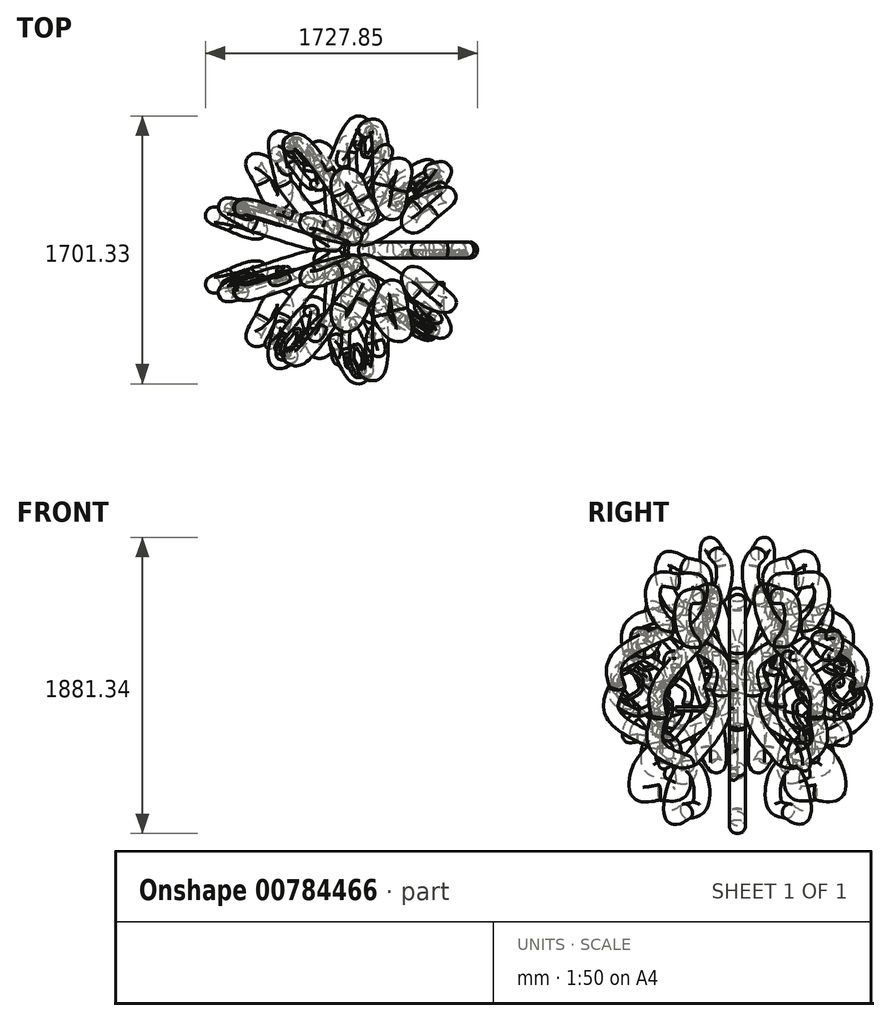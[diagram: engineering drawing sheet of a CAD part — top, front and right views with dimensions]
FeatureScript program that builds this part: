
annotation { "Feature Type Name" : "Feature", "Feature Type Description" : "" }
export const myFeature = defineFeature(function(context is Context, id is Id, definition is map)
    precondition{}
    {
        {
            var Q0;
            Q0=qCreatedBy(makeId("Top.planeOp"),FACE);
            var sketch = newSketch(context, id + "F0", { "sketchPlane" : qUnion([Q0])});
            skEllipse(sketch, "E0", {"center": v(0, 0) * mm, "majorRadius": 51.08 * mm, "minorRadius": 47.34 * mm, "majorAxis": v(-0.2, -0.98)});
            skSolve(sketch);
        }
        {
            var Q0;
            Q0=qCreatedBy(makeId("Front.planeOp"),FACE);
            var sketch = newSketch(context, id + "F1", { "sketchPlane" : qUnion([Q0])});
            skFitSpline(sketch, "E1", {"points": [v(0, 0) * mm, v(0, 227.77) * mm, v(209.25, 339.23) * mm, v(471.17, 411.68) * mm, v(599.35, 548.2) * mm, v(610.5, 656.88) * mm, v(487.9, 693.1) * mm], "startDerivative": vector(-275.49, 1390.88) * mm, "endDerivative": vector(-1128.05, 106.2) * mm});
            skSolve(sketch);
        }
        {
            var Q0;
            Q0=makeQuery(id+"F0.imprint","IMPRINT",FACE,{"disambiguationData":[TD([[makeQuery(id+"F0.imprint","IMPRINT",EDGE,{"derivedFrom":sQuery(id+"F0.wireOp",EDGE,"E0")}),1.0]])]});
            var Q1;
            Q1=sQuery(id+"F1.wireOp",EDGE,"E1");
            sweep(context, id + "F2", {"profiles" : qUnion([Q0]), "path" : qUnion([Q1])});
        }
        {
            var Q0;
            Q0=makeQuery(id+"F2.opSweep","SWEPT_BODY",BODY,{"disambiguationData":[OSD([sQuery(id+"F0.wireOp",EDGE,"E0"),sQuery(id+"F1.wireOp",EDGE,"E1")])]});
            var Q1;
            Q1=makeQuery(id+"F2.opSweep","CAP_FACE",FACE,{"disambiguationData":[OSD([sQuery(id+"F0.wireOp",EDGE,"E0"),sQuery(id+"F1.wireOp",VERTEX,"E1.end")])],"isStart":false});
            mirror(context, id + "F3", {"operationType" : NewBodyOperationType.ADD, "entities" : qUnion([Q0]), "mirrorPlane" : qUnion([Q1])});
        }
        {
            var Q0;
            Q0=qCreatedBy(makeId("Front.planeOp"),FACE);
            var sketch = newSketch(context, id + "F4", { "sketchPlane" : qUnion([Q0])});
            skLineSegment(sketch, "E2", {"start": v(788.67, -179) * mm, "end": v(-324.82, 201.02) * mm});
            skLineSegment(sketch, "E3", {"start": v(-324.82, 201.02) * mm, "end": v(-243.9, -248.34) * mm});
            skLineSegment(sketch, "E4", {"start": v(-243.9, -248.34) * mm, "end": v(620.3, -334.33) * mm});
            skLineSegment(sketch, "E5", {"start": v(620.3, -334.33) * mm, "end": v(788.67, -179) * mm});
            skSolve(sketch);
        }
        {
            var Q0;
            Q0 = qSketchRegion(id + "F4", true);
            extrude(context, id + "F5", {"entities" : qUnion([Q0]), "operationType" : NewBodyOperationType.REMOVE, "endBound" : BoundingType.SYMMETRIC, "depth" : 300 * mm, "offsetDistance" : 25 * mm});
        }
        {
            var Q0;
            Q0=makeQuery(id+"F2.opSweep","SWEPT_BODY",BODY,{"disambiguationData":[OSD([sQuery(id+"F0.wireOp",EDGE,"E0"),sQuery(id+"F1.wireOp",EDGE,"E1")])]});
            var Q1;
            Q1=makeQuery(id+"F5.boolean.opBoolean","COPY",FACE,{"disambiguationData":[TD([makeQuery(id+"F3.opPattern","COPY",FACE,{"derivedFrom":makeQuery(id+"F2.opSweep","SWEPT_FACE",FACE,{"disambiguationData":[OSD([sQuery(id+"F0.wireOp",EDGE,"E0"),sQuery(id+"F1.wireOp",EDGE,"E1")])]}),"instanceName":"1"})])],"derivedFrom":makeQuery(id+"F5.opExtrude","SWEPT_FACE",FACE,{"disambiguationData":[OSD([sQuery(id+"F4.wireOp",EDGE,"E2")])]})});
            mirror(context, id + "F6", {"operationType" : NewBodyOperationType.ADD, "entities" : qUnion([Q0]), "mirrorPlane" : qUnion([Q1])});
        }
        {
            var Q0;
            {var subQ0=sQuery(id+"F0.wireOp",EDGE,"E0");var subQ1=makeQuery(id+"F2.opSweep","SWEPT_FACE",FACE,{"disambiguationData":[OSD([subQ0,sQuery(id+"F1.wireOp",EDGE,"E1")])]});var subQ2=makeQuery(id+"F3.opPattern","COPY",FACE,{"derivedFrom":subQ1,"instanceName":"1"});var subQ3=makeQuery(id+"F5.boolean.opBoolean","INTERSECT",EDGE,{"derivedFrom":[makeQuery(id+"F3.boolean.opBoolean","SPLIT",FACE,{"disambiguationData":[TD([subQ1,makeQuery(id+"F3.opPattern","COPY",FACE,{"derivedFrom":makeQuery(id+"F2.opSweep","CAP_FACE",FACE,{"disambiguationData":[OSD([subQ0,sQuery(id+"F1.wireOp",VERTEX,"E1.start")])],"isStart":true}),"instanceName":"1"}),subQ2])],"derivedFrom":subQ2}),makeQuery(id+"F5.opExtrude","SWEPT_FACE",FACE,{"disambiguationData":[OSD([sQuery(id+"F4.wireOp",EDGE,"E2")])]})]});Q0=makeQuery(id+"F6.boolean.opBoolean","MERGE",EDGE,{"derivedFrom":[subQ3,makeQuery(id+"F6.opPattern","COPY",EDGE,{"derivedFrom":subQ3,"instanceName":"1"})]});}
            fillet(context, id + "F7", {"entities" : qUnion([Q0]), "radius" : 15 * mm, "tangentPropagation" : true, "allowEdgeOverflow" : false});
        }
        {
            var Q0;
            Q0=makeQuery(id+"F2.opSweep","SWEPT_BODY",BODY,{"disambiguationData":[OSD([sQuery(id+"F0.wireOp",EDGE,"E0"),sQuery(id+"F1.wireOp",EDGE,"E1")])]});
            var Q1;
            {var subQ0=sQuery(id+"F0.wireOp",EDGE,"E0");var subQ1=makeQuery(id+"F2.opSweep","SWEPT_FACE",FACE,{"disambiguationData":[OSD([subQ0,sQuery(id+"F1.wireOp",EDGE,"E1")])]});var subQ2=makeQuery(id+"F3.opPattern","COPY",FACE,{"derivedFrom":subQ1,"instanceName":"1"});var subQ3=makeQuery(id+"F3.boolean.opBoolean","SPLIT",FACE,{"disambiguationData":[TD([subQ1,makeQuery(id+"F3.opPattern","COPY",FACE,{"derivedFrom":makeQuery(id+"F2.opSweep","CAP_FACE",FACE,{"disambiguationData":[OSD([subQ0,sQuery(id+"F1.wireOp",VERTEX,"E1.start")])],"isStart":true}),"instanceName":"1"}),subQ2])],"derivedFrom":subQ2});var subQ4=subQ3;var subQ5=makeQuery(id+"F5.boolean.opBoolean","INTERSECT",EDGE,{"derivedFrom":[subQ3,makeQuery(id+"F5.opExtrude","SWEPT_FACE",FACE,{"disambiguationData":[OSD([sQuery(id+"F4.wireOp",EDGE,"E2")])]})]});Q1=makeQuery(id+"F7.opFillet","BLEND_VERTEX",VERTEX,{"disambiguationData":[OD(0.0)],"blendedFrom":[makeQuery(id+"F6.boolean.opBoolean","MERGE",EDGE,{"derivedFrom":[subQ5,makeQuery(id+"F6.opPattern","COPY",EDGE,{"derivedFrom":subQ5,"instanceName":"1"})]}),subQ4,makeQuery(id+"F6.opPattern","COPY",FACE,{"derivedFrom":subQ4,"instanceName":"1"})],"blendedInto":[subQ4,makeQuery(id+"F6.opPattern","COPY",FACE,{"derivedFrom":subQ4,"instanceName":"1"})]});}
            transform(context, id + "F8", {"entities" : qUnion([Q0]), "transformType" : TransformType.SCALE_UNIFORMLY, "scale" : 0.5, "scalePoint" : qUnion([Q1]), "makeCopy" : true});
        }
        {
            var Q0;
            Q0=makeQuery(id+"F8.opPattern","COPY",BODY,{"derivedFrom":makeQuery(id+"F2.opSweep","SWEPT_BODY",BODY,{"disambiguationData":[OSD([sQuery(id+"F0.wireOp",EDGE,"E0"),sQuery(id+"F1.wireOp",EDGE,"E1")])]}),"instanceName":"1"});
            var Q1;
            {var subQ0=sQuery(id+"F0.wireOp",EDGE,"E0");var subQ1=makeQuery(id+"F2.opSweep","SWEPT_FACE",FACE,{"disambiguationData":[OSD([subQ0,sQuery(id+"F1.wireOp",EDGE,"E1")])]});var subQ2=makeQuery(id+"F3.opPattern","COPY",FACE,{"derivedFrom":subQ1,"instanceName":"1"});var subQ3=makeQuery(id+"F3.boolean.opBoolean","SPLIT",FACE,{"disambiguationData":[TD([subQ1,makeQuery(id+"F3.opPattern","COPY",FACE,{"derivedFrom":makeQuery(id+"F2.opSweep","CAP_FACE",FACE,{"disambiguationData":[OSD([subQ0,sQuery(id+"F1.wireOp",VERTEX,"E1.start")])],"isStart":true}),"instanceName":"1"}),subQ2])],"derivedFrom":subQ2});var subQ4=subQ3;var subQ5=makeQuery(id+"F5.boolean.opBoolean","INTERSECT",EDGE,{"derivedFrom":[subQ3,makeQuery(id+"F5.opExtrude","SWEPT_FACE",FACE,{"disambiguationData":[OSD([sQuery(id+"F4.wireOp",EDGE,"E2")])]})]});Q1=makeQuery(id+"F7.opFillet","BLEND_VERTEX",VERTEX,{"disambiguationData":[OD(0.0)],"blendedFrom":[makeQuery(id+"F6.boolean.opBoolean","MERGE",EDGE,{"derivedFrom":[subQ5,makeQuery(id+"F6.opPattern","COPY",EDGE,{"derivedFrom":subQ5,"instanceName":"1"})]}),subQ4,makeQuery(id+"F6.opPattern","COPY",FACE,{"derivedFrom":subQ4,"instanceName":"1"})],"blendedInto":[subQ4,makeQuery(id+"F6.opPattern","COPY",FACE,{"derivedFrom":subQ4,"instanceName":"1"})]});}
            transform(context, id + "F9", {"entities" : qUnion([Q0]), "transformType" : TransformType.SCALE_UNIFORMLY, "scale" : 0.5, "scalePoint" : qUnion([Q1]), "makeCopy" : true});
        }
        {
            var Q0;
            Q0=qCreatedBy(makeId("Front.planeOp"),FACE);
            var sketch = newSketch(context, id + "F10", { "sketchPlane" : qUnion([Q0])});
            skLineSegment(sketch, "E6", {"start": v(-325.42, -210.05) * mm, "end": v(0, 537.04) * mm});
            skSolve(sketch);
        }
        {
            var Q0;
            Q0=makeQuery(id+"F9.opPattern","COPY",BODY,{"derivedFrom":makeQuery(id+"F8.opPattern","COPY",BODY,{"derivedFrom":makeQuery(id+"F2.opSweep","SWEPT_BODY",BODY,{"disambiguationData":[OSD([sQuery(id+"F0.wireOp",EDGE,"E0"),sQuery(id+"F1.wireOp",EDGE,"E1")])]}),"instanceName":"1"}),"instanceName":"1"});
            var Q1;
            Q1=makeQuery(id+"F8.opPattern","COPY",BODY,{"derivedFrom":makeQuery(id+"F2.opSweep","SWEPT_BODY",BODY,{"disambiguationData":[OSD([sQuery(id+"F0.wireOp",EDGE,"E0"),sQuery(id+"F1.wireOp",EDGE,"E1")])]}),"instanceName":"1"});
            var Q2;
            Q2=makeQuery(id+"F2.opSweep","SWEPT_BODY",BODY,{"disambiguationData":[OSD([sQuery(id+"F0.wireOp",EDGE,"E0"),sQuery(id+"F1.wireOp",EDGE,"E1")])]});
            var Q3;
            Q3=sQuery(id+"F10.wireOp",EDGE,"E6");
            circularPattern(context, id + "F11", {"entities" : qUnion([Q0, Q1, Q2]), "axis" : qUnion([Q3]), "angle" : 360 * degree, "instanceCount" : 9, "equalSpace" : true});
        }
        {
            var Q0;
            Q0=qCreatedBy(makeId("Top.planeOp"),FACE);
            var Q1;
            Q1=qCreatedBy(makeId("Top.planeOp"),FACE);
            var sketch = newSketch(context, id + "F12", { "sketchPlane" : qUnion([Q0, Q1])});
            skLineSegment(sketch, "E7.bottom", {"start": v(475.12, -394.22) * mm, "end": v(243.9, -394.22) * mm});
            skLineSegment(sketch, "E7.top", {"start": v(475.12, -206.78) * mm, "end": v(243.9, -206.78) * mm});
            skLineSegment(sketch, "E7.left", {"start": v(475.12, -394.22) * mm, "end": v(475.12, -206.78) * mm});
            skLineSegment(sketch, "E7.right", {"start": v(243.9, -394.22) * mm, "end": v(243.9, -206.78) * mm});
            skSolve(sketch);
        }
        {
            var Q0;
            Q0 = qSketchRegion(id + "F12", true);
            extrude(context, id + "F13", {"entities" : qUnion([Q0]), "depth" : 25 * mm, "offsetDistance" : 25 * mm});
        }
    });
